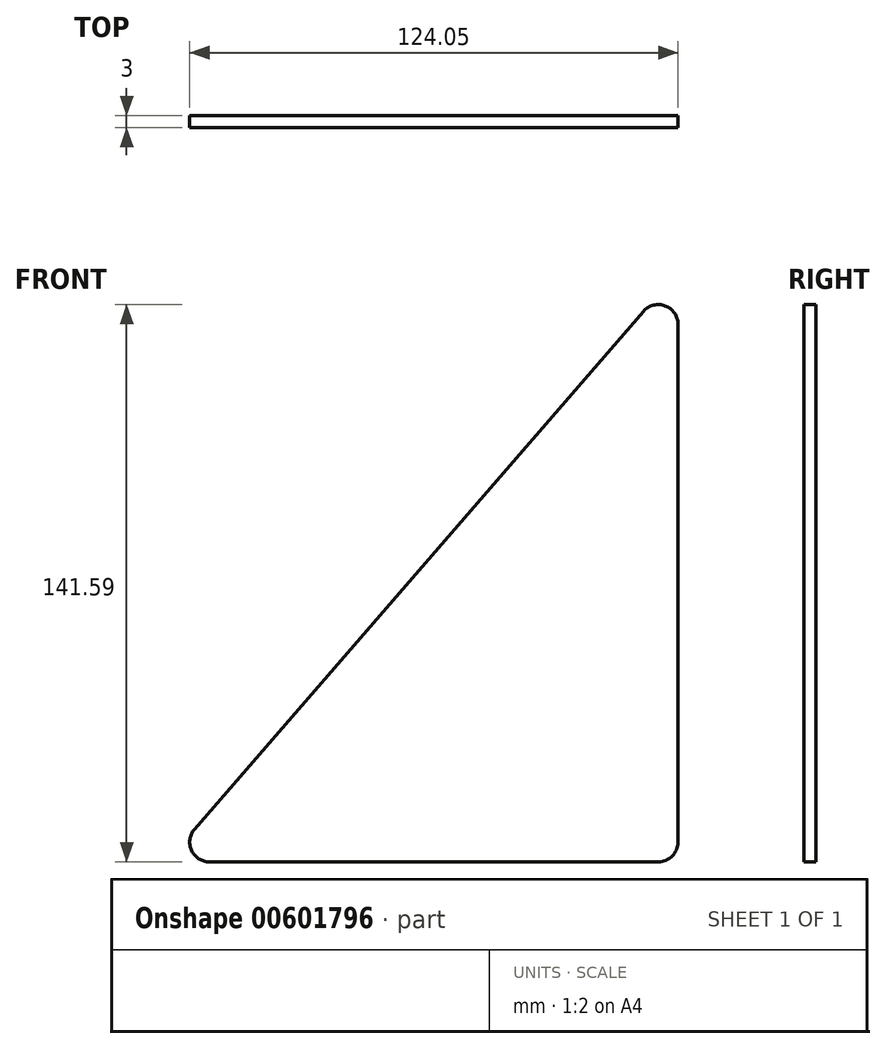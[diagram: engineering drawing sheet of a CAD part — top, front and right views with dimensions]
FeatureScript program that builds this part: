
annotation { "Feature Type Name" : "Feature", "Feature Type Description" : "" }
export const myFeature = defineFeature(function(context is Context, id is Id, definition is map)
    precondition{}
    {
        {
            var Q0;
            Q0=qCreatedBy(makeId("Front.planeOp"),FACE);
            var sketch = newSketch(context, id + "F0", { "sketchPlane" : qUnion([Q0])});
            skLineSegment(sketch, "E0", {"start": v(21.31, 77.56) * mm, "end": v(21.31, -72.44) * mm});
            skLineSegment(sketch, "E1", {"start": v(21.31, -72.44) * mm, "end": v(-108.69, -72.44) * mm});
            skLineSegment(sketch, "E2", {"start": v(-108.69, -72.44) * mm, "end": v(21.31, 77.56) * mm});
            skSolve(sketch);
        }
        {
            var Q0;
            Q0=qSketchRegion(id+"F0",true);
            extrude(context, id + "F1", {"entities" : qUnion([Q0]), "depth" : 3 * mm, "offsetDistance" : 25 * mm});
        }
        {
            var Q0;
            Q0=makeQuery(id+"F1.opExtrude","SWEPT_EDGE",EDGE,{"disambiguationData":[OSD([sQuery(id+"F0.wireOp",EDGE,"E0"),sQuery(id+"F0.wireOp",EDGE,"E2")])]});
            fillet(context, id + "F2", {"entities" : qUnion([Q0]), "radius" : 5 * mm, "tangentPropagation" : true, "allowEdgeOverflow" : false});
        }
        {
            var Q0;
            Q0=makeQuery(id+"F1.opExtrude","SWEPT_EDGE",EDGE,{"disambiguationData":[OSD([sQuery(id+"F0.wireOp",EDGE,"E0"),sQuery(id+"F0.wireOp",EDGE,"E1")])]});
            fillet(context, id + "F3", {"entities" : qUnion([Q0]), "radius" : 5 * mm, "tangentPropagation" : true, "allowEdgeOverflow" : false});
        }
        {
            var Q0;
            Q0=makeQuery(id+"F1.opExtrude","SWEPT_EDGE",EDGE,{"disambiguationData":[OSD([sQuery(id+"F0.wireOp",EDGE,"E1"),sQuery(id+"F0.wireOp",EDGE,"E2")])]});
            fillet(context, id + "F4", {"entities" : qUnion([Q0]), "radius" : 5 * mm, "tangentPropagation" : true, "allowEdgeOverflow" : false});
        }
    });
